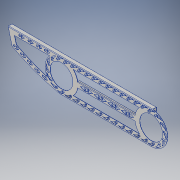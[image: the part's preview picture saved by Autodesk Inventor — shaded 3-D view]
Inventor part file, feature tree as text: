
AUTODESK INVENTOR PART (.ipt)
format: ipt  version: 2016 (Build 200138000, 138)  size: 937,984 bytes
history: native  units: in
note: dims shown in document units (in); Inventor stores cm internally (conversion verified against a paired STEP export)
features: other x18, sheet_metal_op x9, sketch x4
ambient origin geometry x8: Origin, YZ Plane, XZ Plane, XY Plane, X Axis, Y Axis, Z Axis, Center Point
bodies: Solid1 (feature_tree)
feature tree (31):
  other  "Fender Base"
  sheet_metal_op  "Face1"
  other  "Oval Pattern"
  other  "Top flange"
  other  "Mid flange"
  other  "Bottom flange"
  other  "Top flange extension"
  other  "Plate1"
  sketch  "Sketch4"  dims[d0=0.6in]
  other  "Plate2"
  sheet_metal_op  "Bend1"
  sheet_metal_op  "Corner1"
  sketch  "Sketch5"  dims[d1=4.18in]
  other  "Plate3"
  sheet_metal_op  "Bend2"
  sheet_metal_op  "Corner2"
  sketch  "Sketch6"  dims[d2=0.6in]
  other  "Plate4"
  sheet_metal_op  "Bend3"
  sheet_metal_op  "Corner3"
  sketch  "Sketch7"  dims[d3=4.38in d4=0.6in d5=4.18in d6=23.0in d7=0.6in d8=4.28in d9=23.0in d10=7.32in d11=7.32in d13=23.0in d14=1.25in d23=0.0641in d36=2.7559in d38=1.1681in d41=2.7559in d42=5.1181in d44=1.8in d45=0.3937in d47=1.0in d49=2.7559in d51=180.0deg d53=4.7244in d55=1.95in d56=0.3937in d58=1.0in d60=1.25in d61=1.25in d62=0.0641in d63=0.0in d64=0.0641in d65=0.0in d66=1.25in d67=0.0641in d68=0.0in d69=0.7in d70=0.18in d85=1.5748in d87=3.5in d88=0.3937in d90=1.0in d92=0.9in d94=0.2242in d96=6.2in d97=3.0in d99=3.0in d100=34.625in d101=0.25in d102=3.25in d103=25.0in d106=1.25in d107=0.0641in d108=0.0in d109=0.0641in d110=0.0in d111=0.5in d112=0.25in d114=2.7559in d116=5.1181in d118=0.3937in d120=2.7559in d122=4.7244in d124=0.3937in d126=1.5748in d128=0.3937in d129=0.5in d130=0.25in d132=2.7559in d134=5.1181in d136=0.3937in d138=2.7559in d140=4.7244in d142=0.3937in d144=1.5748in d146=0.3937in d147=0.5in d148=0.25in d150=2.7559in d152=5.1181in d154=0.3937in d156=2.7559in d158=4.7244in d160=0.3937in d162=1.5748in d164=0.3937in d165=0.5in d166=0.25in d168=2.7559in d170=5.1181in d172=0.3937in d174=2.7559in d176=4.7244in d178=0.3937in d180=1.5748in d182=0.3937in d183=0.5in d184=0.25in d186=2.7559in d188=5.1181in d190=0.3937in d192=2.7559in d194=4.7244in d196=0.3937in d198=1.5748in d200=0.3937in d201=0.5in d202=0.25in d205=2.7559in d207=5.1181in d209=0.3937in d211=2.7559in d213=4.7244in d215=0.3937in d217=1.5748in d219=0.3937in d220=0.5in d221=0.25in d223=2.7559in d225=5.1181in d227=0.3937in d229=2.7559in d231=4.7244in d233=0.3937in d235=1.5748in d237=0.3937in d238=0.5in d239=0.25in d241=2.7559in d243=5.1181in d245=0.3937in d247=2.7559in d249=4.7244in d251=0.3937in d253=1.5748in d255=0.3937in d256=0.5in d257=0.25in d259=2.7559in d261=5.1181in d263=0.3937in d265=2.7559in d267=4.7244in d269=0.3937in d271=1.5748in d273=0.3937in d278=0.85in d279=0.015in d280=0.75in d283=0.0641in d284=0.0in d285=0.0641in d286=0.0641in d287=0.1282in d288=0.0641in d289=1.0in d290=90.0deg d291=0.0641in d292=0.2564in d293=0.0641in d294=0.0641in d295=0.0641in d296=0.0641in d297=0.1282in d298=0.0641in d299=0.5in d300=90.0deg d301=0.0641in d302=0.2564in d303=0.0641in d304=0.0641in d305=0.0641in d306=0.0641in d307=0.1282in d308=0.0641in d309=1.0in d310=90.0deg d311=0.0641in d312=0.2564in d313=0.0641in d314=0.0641in d315=0.0641in d316=0.0641in d317=0.1282in d318=0.0641in d319=1.0in d320=90.0deg d321=0.0641in d322=0.2564in d323=0.0641in d324=0.0641in d325=10.0in d326=0.0in]
  other  "Plate5"
  sheet_metal_op  "Bend4"
  sheet_metal_op  "Corner4"
  other  "Cut1"
  other  "Cut2"
  other  "Cut3"
  other  "Rear Interior"
  other  "Front Patter"
  other  "Rear Pattern"
  other  "Definition1"
